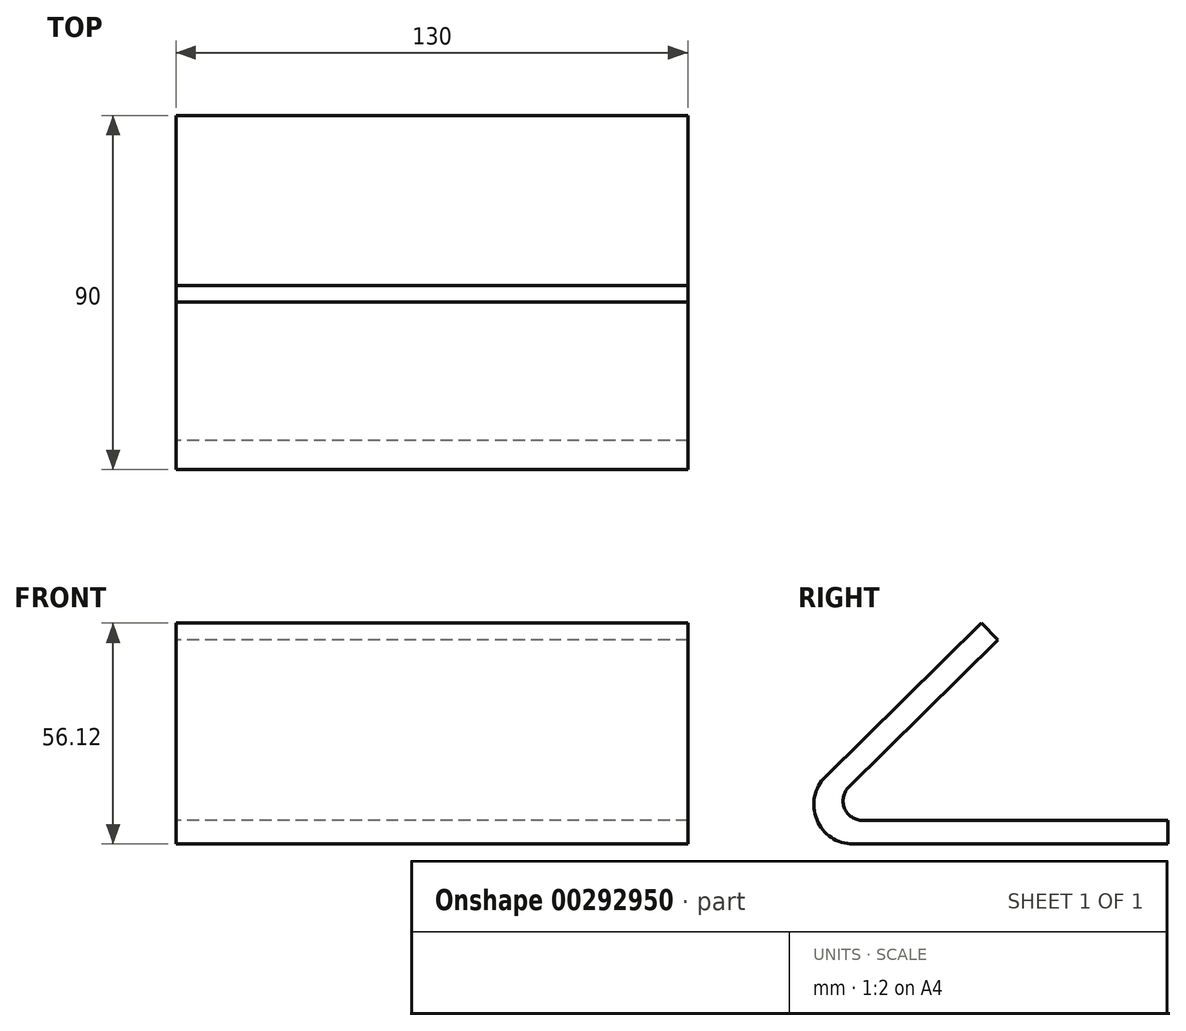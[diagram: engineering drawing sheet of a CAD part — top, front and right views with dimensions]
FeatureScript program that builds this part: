
annotation { "Feature Type Name" : "Feature", "Feature Type Description" : "" }
export const myFeature = defineFeature(function(context is Context, id is Id, definition is map)
    precondition{}
    {
        {
            var Q0;
            Q0=qCreatedBy(makeId("Right.planeOp"),FACE);
            var sketch = newSketch(context, id + "F0", { "sketchPlane" : qUnion([Q0])});
            skLineSegment(sketch, "E0", {"start": v(12.02, 56.12) * mm, "end": v(-27.6, 17.13) * mm});
            skLineSegment(sketch, "E1", {"start": v(-20.58, 0) * mm, "end": v(59.42, 0) * mm});
            skPoint(sketch, "E2.visualSharp", {"position": v(-45, 0) * mm});
            skArc(sketch, "E2.filletArc", {"start": v(-27.6, 17.13) * mm, "mid": v(-29.84, 6.2) * mm, "end": v(-20.58, 0) * mm});
            skLineSegment(sketch, "E3", {"start": v(-21.65, 14.56) * mm, "end": v(16.23, 51.85) * mm});
            skLineSegment(sketch, "E4", {"start": v(-18.14, 6) * mm, "end": v(59.42, 6) * mm});
            skPoint(sketch, "E5.visualSharp", {"position": v(-30.35, 6) * mm});
            skArc(sketch, "E5.filletArc", {"start": v(-21.65, 14.56) * mm, "mid": v(-22.77, 9.1) * mm, "end": v(-18.14, 6) * mm});
            skLineSegment(sketch, "E6", {"start": v(59.42, 0) * mm, "end": v(59.42, 6) * mm});
            skLineSegment(sketch, "E7", {"start": v(12.02, 56.12) * mm, "end": v(16.23, 51.85) * mm});
            skSolve(sketch);
        }
        {
            var Q0;
            Q0 = qSketchRegion(id + "F0", true);
            extrude(context, id + "F1", {"entities" : qUnion([Q0]), "depth" : 130 * mm});
        }
    });
